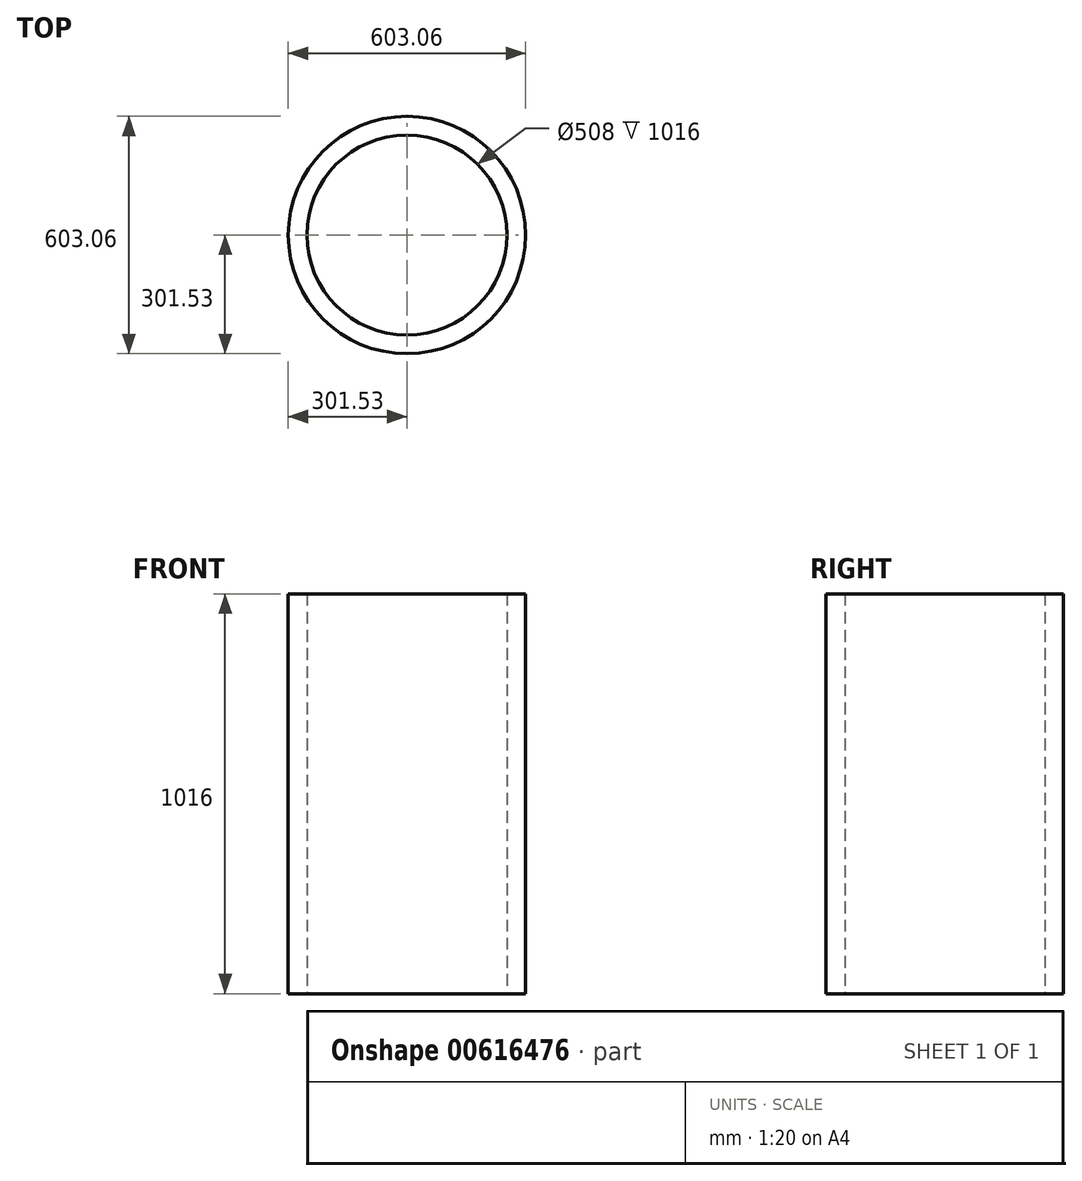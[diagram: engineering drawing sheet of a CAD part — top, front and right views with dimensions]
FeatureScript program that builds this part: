
annotation { "Feature Type Name" : "Feature", "Feature Type Description" : "" }
export const myFeature = defineFeature(function(context is Context, id is Id, definition is map)
    precondition{}
    {
        {
            var Q0;
            Q0=qCreatedBy(makeId("Top.planeOp"),FACE);
            var sketch = newSketch(context, id + "F0", { "sketchPlane" : qUnion([Q0])});
            skCircle(sketch, "E0", {"center": v(0, 0) * mm, "radius": 254 * mm});
            skSolve(sketch);
        }
        {
            var Q0;
            Q0=makeQuery(id+"F0.imprint","IMPRINT",FACE,{"disambiguationData":[TD([[makeQuery(id+"F0.imprint","IMPRINT",EDGE,{"derivedFrom":sQuery(id+"F0.wireOp",EDGE,"E0")}),1.0]])]});
            var sketch = newSketch(context, id + "F1", { "sketchPlane" : qUnion([Q0])});
            skCircle(sketch, "E1", {"center": v(0, 0) * mm, "radius": 301.53 * mm});
            skSolve(sketch);
        }
        {
            var Q0;
            Q0=makeQuery(id+"F1.imprint","IMPRINT",FACE,{"disambiguationData":[TD([[makeQuery(id+"F1.imprint","IMPRINT",EDGE,{"derivedFrom":sQuery(id+"F1.wireOp",EDGE,"E1")}),1.0]])]});
            extrude(context, id + "F2", {"entities" : qUnion([Q0]), "depth" : 1016 * mm, "offsetDistance" : 25.4 * mm});
        }
    });
